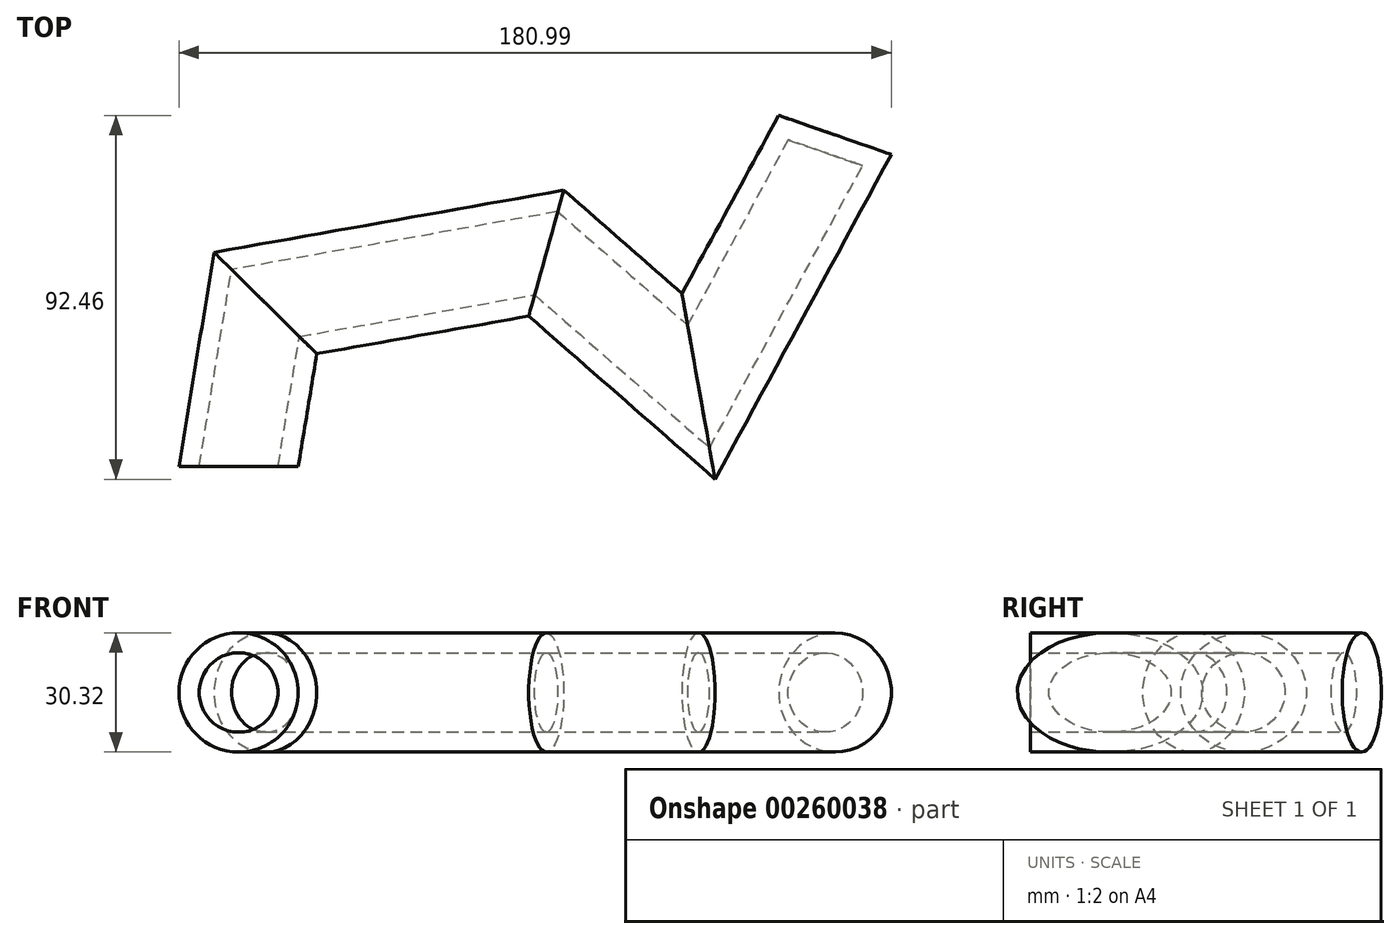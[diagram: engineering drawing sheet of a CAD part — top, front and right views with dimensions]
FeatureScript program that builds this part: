
annotation { "Feature Type Name" : "Feature", "Feature Type Description" : "" }
export const myFeature = defineFeature(function(context is Context, id is Id, definition is map)
    precondition{}
    {
        {
            var Q0;
            Q0=qCreatedBy(makeId("Top.planeOp"),FACE);
            var sketch = newSketch(context, id + "F0", { "sketchPlane" : qUnion([Q0])});
            skLineSegment(sketch, "E0", {"start": v(-87.64, -34.5) * mm, "end": v(-80.93, 6.41) * mm});
            skLineSegment(sketch, "E1", {"start": v(-80.93, 6.41) * mm, "end": v(-10.38, 18.93) * mm});
            skLineSegment(sketch, "E2", {"start": v(-10.38, 18.93) * mm, "end": v(28.7, -15.27) * mm});
            skLineSegment(sketch, "E3", {"start": v(28.7, -15.27) * mm, "end": v(63.82, 49.47) * mm});
            skSolve(sketch);
        }
        {
            var Q0;
            Q0=qCreatedBy(makeId("Front.planeOp"),FACE);
            var Q1;
            Q1=sQuery(id+"F0.wireOp",VERTEX,"E0.start");
            cPlane(context, id + "F1", {"entities" : qUnion([Q0, Q1]), "cplaneType" : CPlaneType.PLANE_POINT, "offset" : 25.4 * mm, "width" : 152.4 * mm, "height" : 152.4 * mm});
        }
        {
            var Q0;
            Q0=qCreatedBy(id+"F1.planeOp",FACE);
            var sketch = newSketch(context, id + "F2", { "sketchPlane" : qUnion([Q0])});
            skCircle(sketch, "E4", {"center": v(-88.33, 0) * mm, "radius": 15.16 * mm});
            skSolve(sketch);
        }
        {
            var Q0;
            Q0=makeQuery(id+"F2.imprint","IMPRINT",FACE,{"disambiguationData":[TD([[makeQuery(id+"F2.imprint","IMPRINT",EDGE,{"derivedFrom":sQuery(id+"F2.wireOp",EDGE,"E4")}),1.0]])]});
            var Q1;
            Q1=sQuery(id+"F0.wireOp",EDGE,"E0");
            var Q2;
            Q2=sQuery(id+"F0.wireOp",EDGE,"E1");
            var Q3;
            Q3=sQuery(id+"F0.wireOp",EDGE,"E2");
            var Q4;
            Q4=sQuery(id+"F0.wireOp",EDGE,"E3");
            sweep(context, id + "F3", {"profiles" : qUnion([Q0]), "path" : qUnion([Q1, Q2, Q3, Q4])});
        }
        {
            var Q0;
            Q0=makeQuery(id+"F3.opSweep","CAP_FACE",FACE,{"disambiguationData":[OSD([sQuery(id+"F0.wireOp",VERTEX,"E0.start"),sQuery(id+"F2.wireOp",EDGE,"E4")])],"isStart":true});
            shell(context, id + "F4", {"entities" : qUnion([Q0]), "thickness" : 5.08 * mm});
        }
    });
